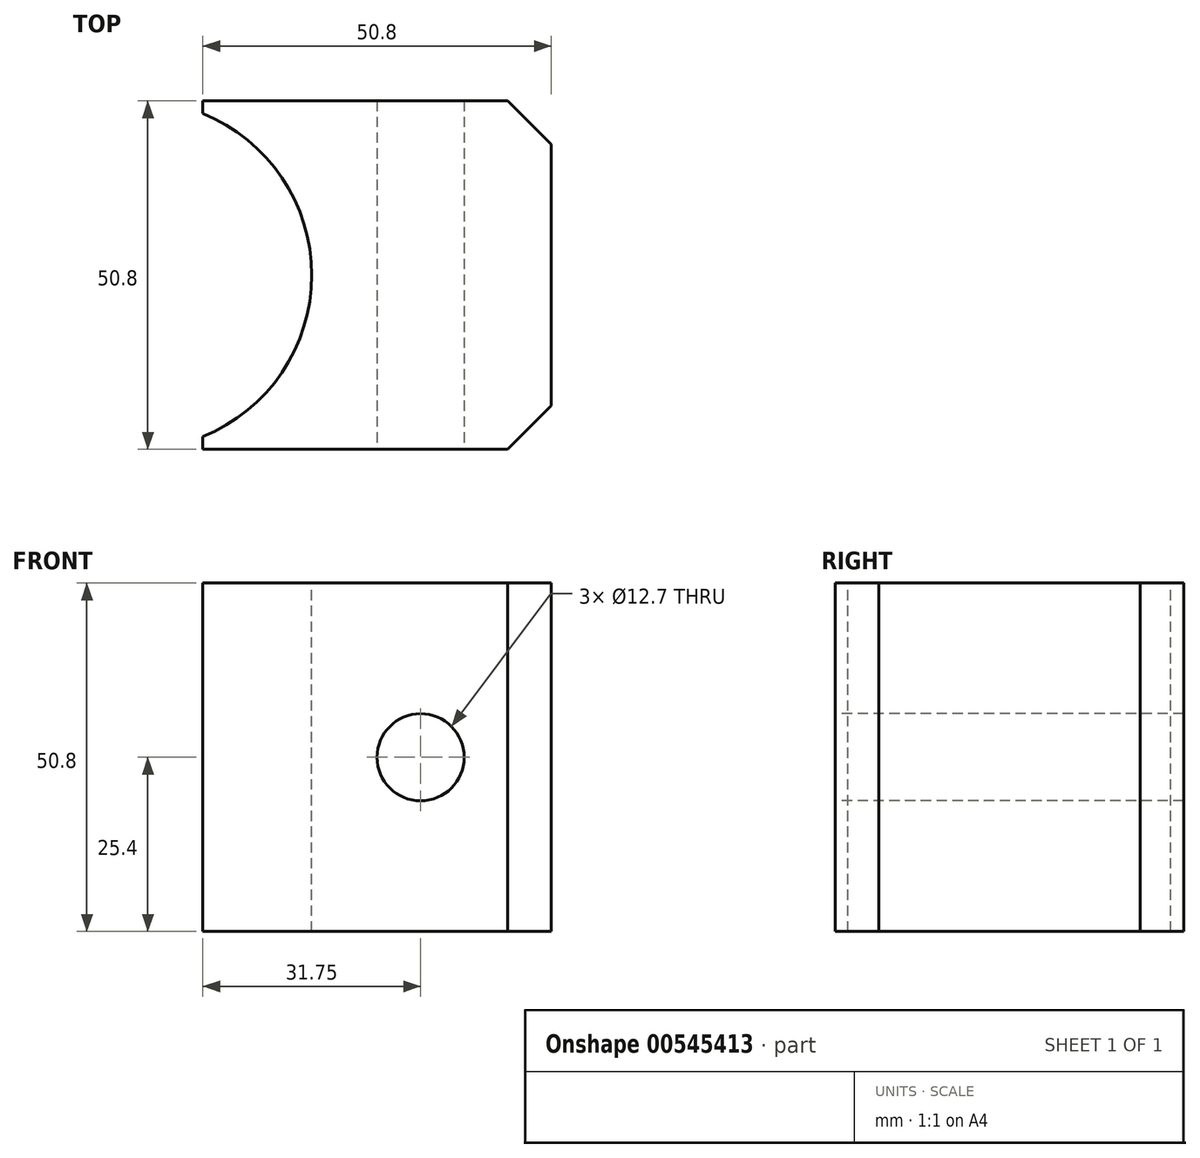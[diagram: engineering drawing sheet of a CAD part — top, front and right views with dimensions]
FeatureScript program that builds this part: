
annotation { "Feature Type Name" : "Feature", "Feature Type Description" : "" }
export const myFeature = defineFeature(function(context is Context, id is Id, definition is map)
    precondition{}
    {
        {
            var Q0;
            Q0=qCreatedBy(makeId("Front.planeOp"),FACE);
            var sketch = newSketch(context, id + "F0", { "sketchPlane" : qUnion([Q0])});
            skLineSegment(sketch, "E0.bottom", {"start": v(25.4, -25.4) * mm, "end": v(-25.4, -25.4) * mm});
            skLineSegment(sketch, "E0.top", {"start": v(25.4, 25.4) * mm, "end": v(-25.4, 25.4) * mm});
            skLineSegment(sketch, "E0.left", {"start": v(25.4, -25.4) * mm, "end": v(25.4, 25.4) * mm});
            skLineSegment(sketch, "E0.right", {"start": v(-25.4, -25.4) * mm, "end": v(-25.4, 25.4) * mm});
            skPoint(sketch, "E0.middle", {"position": v(0, 0) * mm});
            skSolve(sketch);
        }
        {
            var Q0;
            Q0=makeQuery(id+"F0.imprint","IMPRINT",FACE,{"disambiguationData":[TD([[makeQuery(id+"F0.imprint","IMPRINT",EDGE,{"derivedFrom":sQuery(id+"F0.wireOp",EDGE,"E0.bottom")}),-1.0]])]});
            extrude(context, id + "F1", {"entities" : qUnion([Q0]), "endBound" : BoundingType.SYMMETRIC, "depth" : 50.8 * mm, "offsetDistance" : 25.4 * mm});
        }
        {
            var Q0;
            Q0=makeQuery(id+"F1.opExtrude","SWEPT_FACE",FACE,{"disambiguationData":[OSD([sQuery(id+"F0.wireOp",EDGE,"E0.top")])]});
            var sketch = newSketch(context, id + "F2", { "sketchPlane" : qUnion([Q0])});
            skCircle(sketch, "E1", {"center": v(-34.93, 0) * mm, "radius": 25.4 * mm});
            skPoint(sketch, "E1.centerSnap0", {"position": v(-25.4, 0) * mm});
            skSolve(sketch);
        }
        {
            var Q0;
            {var subQ0=sQuery(id+"F2.wireOp",EDGE,"E1");var subQ1=makeQuery(id+"F1.opExtrude","SWEPT_EDGE",EDGE,{"disambiguationData":[OSD([sQuery(id+"F0.wireOp",EDGE,"E0.top"),sQuery(id+"F0.wireOp",EDGE,"E0.right")])]});var subQ2=makeQuery(id+"F2.imprint","INTERSECT",VERTEX,{"disambiguationData":[OD(0.0)],"derivedFrom":[subQ1,subQ0]});Q0=makeQuery(id+"F2.imprint","IMPRINT",FACE,{"disambiguationData":[TD([[makeQuery(id+"F2.imprint","IMPRINT",EDGE,{"disambiguationData":[TD([[subQ2,1.0]])],"derivedFrom":subQ0}),1.0]])]});}
            extrude(context, id + "F3", {"entities" : qUnion([Q0]), "operationType" : NewBodyOperationType.REMOVE, "oppositeDirection" : true, "depth" : 50.8 * mm, "offsetDistance" : 25.4 * mm});
        }
        {
            var Q0;
            Q0=makeQuery(id+"F1.opExtrude","CAP_EDGE",EDGE,{"disambiguationData":[OSD([sQuery(id+"F0.wireOp",EDGE,"E0.left")])],"isStart":false});
            var Q1;
            Q1=makeQuery(id+"F1.opExtrude","CAP_EDGE",EDGE,{"disambiguationData":[OSD([sQuery(id+"F0.wireOp",EDGE,"E0.left")])],"isStart":true});
            chamfer(context, id + "F4", {"entities" : qUnion([Q0, Q1]), "width" : 6.35 * mm, "tangentPropagation" : true});
        }
        {
            var Q0;
            Q0=makeQuery(id+"F1.opExtrude","CAP_FACE",FACE,{"disambiguationData":[OSD([sQuery(id+"F0.wireOp",EDGE,"E0.bottom"),sQuery(id+"F0.wireOp",EDGE,"E0.top"),sQuery(id+"F0.wireOp",EDGE,"E0.left"),sQuery(id+"F0.wireOp",EDGE,"E0.right")])],"isStart":false});
            var sketch = newSketch(context, id + "F5", { "sketchPlane" : qUnion([Q0])});
            skCircle(sketch, "E2", {"center": v(6.35, 0) * mm, "radius": 6.35 * mm});
            skSolve(sketch);
        }
        {
            var Q0;
            Q0=makeQuery(id+"F5.imprint","IMPRINT",FACE,{"disambiguationData":[TD([[makeQuery(id+"F5.imprint","IMPRINT",EDGE,{"derivedFrom":sQuery(id+"F5.wireOp",EDGE,"E2")}),1.0]])]});
            extrude(context, id + "F6", {"entities" : qUnion([Q0]), "operationType" : NewBodyOperationType.REMOVE, "endBound" : BoundingType.THROUGH_ALL, "oppositeDirection" : true, "depth" : 25.4 * mm, "offsetDistance" : 25.4 * mm});
        }
    });
